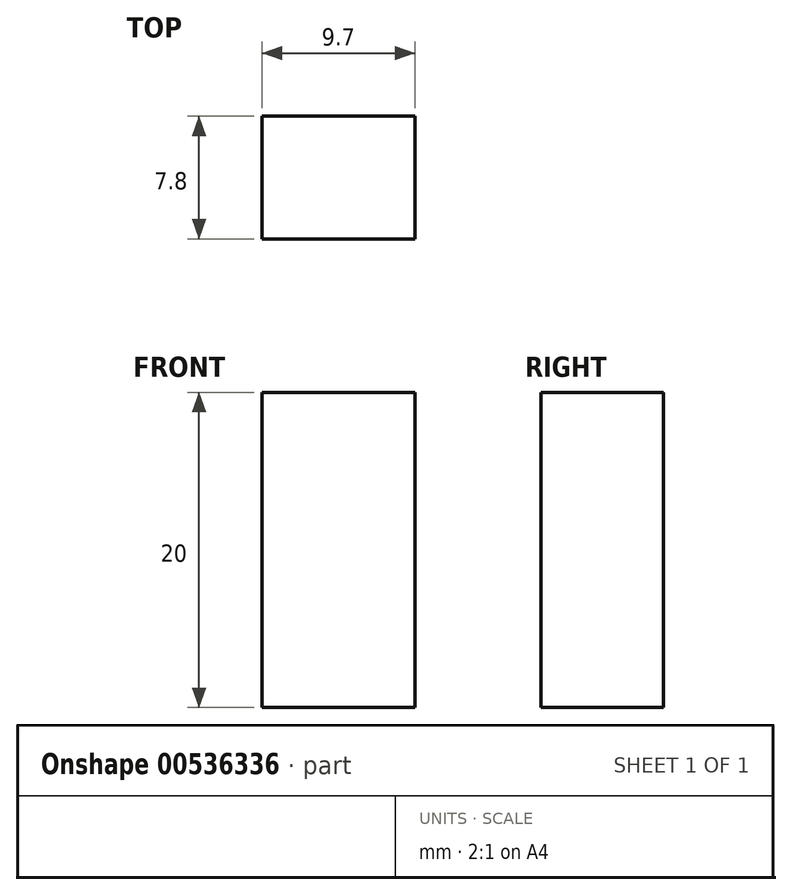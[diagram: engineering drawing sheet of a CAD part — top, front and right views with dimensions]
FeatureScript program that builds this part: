
annotation { "Feature Type Name" : "Feature", "Feature Type Description" : "" }
export const myFeature = defineFeature(function(context is Context, id is Id, definition is map)
    precondition{}
    {
        {
            var Q0;
            Q0=qCreatedBy(makeId("Top.planeOp"),FACE);
            var sketch = newSketch(context, id + "F0", { "sketchPlane" : qUnion([Q0])});
            skLineSegment(sketch, "E0.bottom", {"start": v(4.85, -3.9) * mm, "end": v(-4.85, -3.9) * mm});
            skLineSegment(sketch, "E0.top", {"start": v(4.85, 3.9) * mm, "end": v(-4.85, 3.9) * mm});
            skLineSegment(sketch, "E0.left", {"start": v(4.85, -3.9) * mm, "end": v(4.85, 3.9) * mm});
            skLineSegment(sketch, "E0.right", {"start": v(-4.85, -3.9) * mm, "end": v(-4.85, 3.9) * mm});
            skPoint(sketch, "E0.middle", {"position": v(0, 0) * mm});
            skSolve(sketch);
        }
        {
            var Q0;
            Q0 = qSketchRegion(id + "F0", true);
            extrude(context, id + "F1", {"entities" : qUnion([Q0]), "depth" : 20 * mm, "offsetDistance" : 25 * mm});
        }
    });
